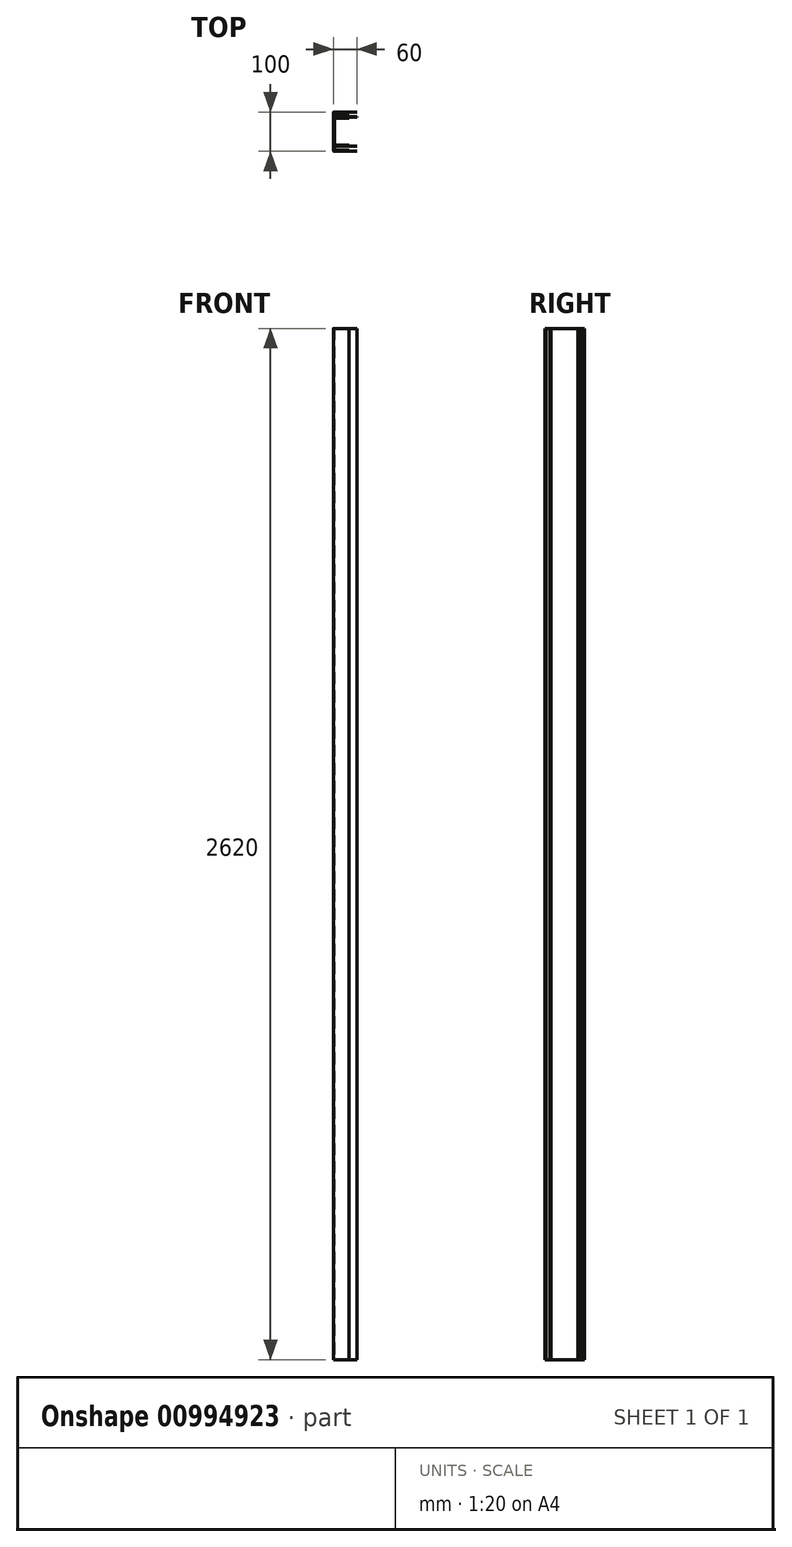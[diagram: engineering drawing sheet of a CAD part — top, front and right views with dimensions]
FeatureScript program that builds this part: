
annotation { "Feature Type Name" : "Feature", "Feature Type Description" : "" }
export const myFeature = defineFeature(function(context is Context, id is Id, definition is map)
    precondition{}
    {
        {
            var Q0;
            Q0=qCreatedBy(makeId("Top.planeOp"),FACE);
            var sketch = newSketch(context, id + "F0", { "sketchPlane" : qUnion([Q0])});
            skLineSegment(sketch, "E0.bottom", {"start": v(3, 37.5) * mm, "end": v(40, 37.5) * mm});
            skLineSegment(sketch, "E0.top", {"start": v(3, -37.5) * mm, "end": v(40, -37.5) * mm});
            skLineSegment(sketch, "E0.left", {"start": v(0, 34.5) * mm, "end": v(0, -34.5) * mm});
            skPoint(sketch, "E1", {"position": v(0, 0) * mm});
            skLineSegment(sketch, "E2.0", {"start": v(4, 34.5) * mm, "end": v(40, 34.5) * mm});
            skLineSegment(sketch, "E2.1", {"start": v(3, 33.5) * mm, "end": v(3, -33.5) * mm});
            skLineSegment(sketch, "E2.2", {"start": v(4, -34.5) * mm, "end": v(40, -34.5) * mm});
            skLineSegment(sketch, "E3", {"start": v(40, 37.5) * mm, "end": v(40, 34.5) * mm});
            skLineSegment(sketch, "E4", {"start": v(40, -34.5) * mm, "end": v(40, -37.5) * mm});
            skPoint(sketch, "E5.visualSharp", {"position": v(3, 34.5) * mm});
            skArc(sketch, "E5.filletArc", {"start": v(4, 34.5) * mm, "mid": v(3.3, 34.2) * mm, "end": v(3, 33.5) * mm});
            skPoint(sketch, "E6.visualSharp", {"position": v(3, -34.5) * mm});
            skArc(sketch, "E6.filletArc", {"start": v(3, -33.5) * mm, "mid": v(3.3, -34.2) * mm, "end": v(4, -34.5) * mm});
            skPoint(sketch, "E7.visualSharp", {"position": v(0, 37.5) * mm});
            skArc(sketch, "E7.filletArc", {"start": v(3, 37.5) * mm, "mid": v(0.88, 36.62) * mm, "end": v(0, 34.5) * mm});
            skPoint(sketch, "E8.visualSharp", {"position": v(0, -37.5) * mm});
            skArc(sketch, "E8.filletArc", {"start": v(0, -34.5) * mm, "mid": v(0.88, -36.62) * mm, "end": v(3, -37.5) * mm});
            skSolve(sketch);
        }
        {
            var Q0;
            Q0 = qSketchRegion(id + "F0", true);
            extrude(context, id + "F1", {"entities" : qUnion([Q0]), "depth" : 2620 * mm, "offsetDistance" : 25 * mm});
        }
        {
            var Q0;
            Q0=qCreatedBy(makeId("Top.planeOp"),FACE);
            var sketch = newSketch(context, id + "F2", { "sketchPlane" : qUnion([Q0])});
            skLineSegment(sketch, "E9.bottom", {"start": v(3, 50) * mm, "end": v(40, 50) * mm});
            skLineSegment(sketch, "E9.top", {"start": v(3, -50) * mm, "end": v(40, -50) * mm});
            skLineSegment(sketch, "E9.left", {"start": v(0, 47) * mm, "end": v(0, -47) * mm});
            skPoint(sketch, "E10", {"position": v(0, 0) * mm});
            skLineSegment(sketch, "E11.0", {"start": v(4, 47) * mm, "end": v(40, 47) * mm});
            skLineSegment(sketch, "E11.1", {"start": v(3, 46) * mm, "end": v(3, -46) * mm});
            skLineSegment(sketch, "E11.2", {"start": v(4, -47) * mm, "end": v(40, -47) * mm});
            skLineSegment(sketch, "E12", {"start": v(40, 50) * mm, "end": v(40, 47) * mm});
            skLineSegment(sketch, "E13", {"start": v(40, -47) * mm, "end": v(40, -50) * mm});
            skPoint(sketch, "E14.visualSharp", {"position": v(3, 47) * mm});
            skArc(sketch, "E14.filletArc", {"start": v(4, 47) * mm, "mid": v(3.3, 46.7) * mm, "end": v(3, 46) * mm});
            skPoint(sketch, "E15.visualSharp", {"position": v(3, -47) * mm});
            skArc(sketch, "E15.filletArc", {"start": v(3, -46) * mm, "mid": v(3.3, -46.7) * mm, "end": v(4, -47) * mm});
            skPoint(sketch, "E16.visualSharp", {"position": v(0, 50) * mm});
            skArc(sketch, "E16.filletArc", {"start": v(3, 50) * mm, "mid": v(0.88, 49.12) * mm, "end": v(0, 47) * mm});
            skPoint(sketch, "E17.visualSharp", {"position": v(0, -50) * mm});
            skArc(sketch, "E17.filletArc", {"start": v(0, -47) * mm, "mid": v(0.88, -49.12) * mm, "end": v(3, -50) * mm});
            skSolve(sketch);
        }
        {
            var Q0;
            Q0 = qSketchRegion(id + "F2", true);
            extrude(context, id + "F3", {"entities" : qUnion([Q0]), "depth" : 2620 * mm, "offsetDistance" : 25 * mm});
        }
        {
            var Q0;
            Q0=qCreatedBy(makeId("Top.planeOp"),FACE);
            var sketch = newSketch(context, id + "F4", { "sketchPlane" : qUnion([Q0])});
            skLineSegment(sketch, "E18.bottom", {"start": v(1, 37.5) * mm, "end": v(60, 37.5) * mm});
            skLineSegment(sketch, "E18.top", {"start": v(1, -37.5) * mm, "end": v(60, -37.5) * mm});
            skLineSegment(sketch, "E18.left", {"start": v(0, 36.5) * mm, "end": v(0, -36.5) * mm});
            skPoint(sketch, "E19", {"position": v(0, 0) * mm});
            skLineSegment(sketch, "E20.0", {"start": v(1.1, 36.9) * mm, "end": v(60, 36.9) * mm});
            skLineSegment(sketch, "E20.1", {"start": v(0.6, 36.4) * mm, "end": v(0.6, -36.4) * mm});
            skLineSegment(sketch, "E20.2", {"start": v(1.1, -36.9) * mm, "end": v(60, -36.9) * mm});
            skLineSegment(sketch, "E21", {"start": v(60, 37.5) * mm, "end": v(60, 36.9) * mm});
            skLineSegment(sketch, "E22", {"start": v(60, -36.9) * mm, "end": v(60, -37.5) * mm});
            skPoint(sketch, "E23.visualSharp", {"position": v(0.6, 36.9) * mm});
            skArc(sketch, "E23.filletArc", {"start": v(1.1, 36.9) * mm, "mid": v(0.75, 36.75) * mm, "end": v(0.6, 36.4) * mm});
            skPoint(sketch, "E24.visualSharp", {"position": v(0.6, -36.9) * mm});
            skArc(sketch, "E24.filletArc", {"start": v(0.6, -36.4) * mm, "mid": v(0.75, -36.75) * mm, "end": v(1.1, -36.9) * mm});
            skPoint(sketch, "E25.visualSharp", {"position": v(0, 37.5) * mm});
            skArc(sketch, "E25.filletArc", {"start": v(1, 37.5) * mm, "mid": v(0.3, 37.2) * mm, "end": v(0, 36.5) * mm});
            skPoint(sketch, "E26.visualSharp", {"position": v(0, -37.5) * mm});
            skArc(sketch, "E26.filletArc", {"start": v(0, -36.5) * mm, "mid": v(0.3, -37.2) * mm, "end": v(1, -37.5) * mm});
            skSolve(sketch);
        }
        {
            var Q0;
            Q0 = qSketchRegion(id + "F4", true);
            extrude(context, id + "F5", {"entities" : qUnion([Q0]), "depth" : 2620 * mm, "offsetDistance" : 25 * mm});
        }
        {
            var Q0;
            Q0=qCreatedBy(makeId("Top.planeOp"),FACE);
            var sketch = newSketch(context, id + "F6", { "sketchPlane" : qUnion([Q0])});
            skLineSegment(sketch, "E27.bottom", {"start": v(1, 50) * mm, "end": v(60, 50) * mm});
            skLineSegment(sketch, "E27.top", {"start": v(1, -50) * mm, "end": v(60, -50) * mm});
            skLineSegment(sketch, "E27.left", {"start": v(0, 49) * mm, "end": v(0, -49) * mm});
            skPoint(sketch, "E28", {"position": v(0, 0) * mm});
            skLineSegment(sketch, "E29.0", {"start": v(1.1, 49.4) * mm, "end": v(60, 49.4) * mm});
            skLineSegment(sketch, "E29.1", {"start": v(0.6, 48.9) * mm, "end": v(0.6, -48.9) * mm});
            skLineSegment(sketch, "E29.2", {"start": v(1.1, -49.4) * mm, "end": v(60, -49.4) * mm});
            skLineSegment(sketch, "E30", {"start": v(60, 50) * mm, "end": v(60, 49.4) * mm});
            skLineSegment(sketch, "E31", {"start": v(60, -49.4) * mm, "end": v(60, -50) * mm});
            skPoint(sketch, "E32.visualSharp", {"position": v(0.6, 49.4) * mm});
            skArc(sketch, "E32.filletArc", {"start": v(1.1, 49.4) * mm, "mid": v(0.75, 49.25) * mm, "end": v(0.6, 48.9) * mm});
            skPoint(sketch, "E33.visualSharp", {"position": v(0.6, -49.4) * mm});
            skArc(sketch, "E33.filletArc", {"start": v(0.6, -48.9) * mm, "mid": v(0.75, -49.25) * mm, "end": v(1.1, -49.4) * mm});
            skPoint(sketch, "E34.visualSharp", {"position": v(0, 50) * mm});
            skArc(sketch, "E34.filletArc", {"start": v(1, 50) * mm, "mid": v(0.3, 49.7) * mm, "end": v(0, 49) * mm});
            skPoint(sketch, "E35.visualSharp", {"position": v(0, -50) * mm});
            skArc(sketch, "E35.filletArc", {"start": v(0, -49) * mm, "mid": v(0.3, -49.7) * mm, "end": v(1, -50) * mm});
            skSolve(sketch);
        }
        {
            var Q0;
            Q0 = qSketchRegion(id + "F6", true);
            extrude(context, id + "F7", {"entities" : qUnion([Q0]), "depth" : 2620 * mm, "offsetDistance" : 25 * mm});
        }
    });
